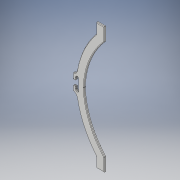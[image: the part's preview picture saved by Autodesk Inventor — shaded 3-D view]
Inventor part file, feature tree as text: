
AUTODESK INVENTOR PART (.ipt)
format: ipt  version: 2018 (Build 220112000, 112)  size: 517,120 bytes
history: native  units: mm
features: extrude x3, sketch x3, fillet x2, mirror x1
ambient origin geometry x8: Origin, YZ Plane, XZ Plane, XY Plane, X Axis, Y Axis, Z Axis, Center Point
bodies: Volumenkörper1 (feature_tree)
feature tree (9):
  extrude  "Extrusion1"  Depth=15.0mm
  mirror  "Spiegeln1"
  extrude  "Extrusion2"  TaperAngle=0.0deg  [1 undecoded]
  fillet  "Rundung1"  Radius=120.0mm
  fillet  "Rundung2"  Radius=150.0mm
  extrude  "Extrusion3"  Depth=15.0mm
  sketch  "Skizze1"  dims[d0=25.0mm d2=15.0mm]
  sketch  "Skizze2"  dims[d4=54.0mm d5=0.0mm d6=120.0mm d7=150.0mm]
  sketch  "Skizze3"  dims[d9=5.0mm d10=15.0mm d11=15.0mm d12=4.0mm d13=0.0mm d15=10.0mm d16=5.0mm d17=10.0mm d18=5.0mm d19=5.0mm d20=24.0mm d21=4.5mm d22=4.0mm d23=0.0mm d24=10.0mm d25=1.0mm d26=1.0mm d27=0.0mm]
note: 1 required parameter value undecoded (feature->parameter linkage not recoverable at this tier; creation-order binding heuristic only, values carry confidence <= 0.55)
